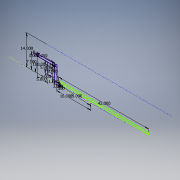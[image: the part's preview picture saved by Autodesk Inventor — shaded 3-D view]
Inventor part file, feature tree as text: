
AUTODESK INVENTOR PART (.ipt)
format: ipt  version: 2017 SP1 (Build 210196100, 196)  size: 114,688 bytes
history: native  units: in
note: dims shown in document units (in); Inventor stores cm internally (conversion verified against a paired STEP export)
features: sketch x1
ambient origin geometry x8: Origin, YZ Plane, XZ Plane, XY Plane, X Axis, Y Axis, Z Axis, Center Point
feature tree (1):
  sketch  "Sketch1"  dims[d0=5.0in d1=2.0in d3=1.0in d4=5.0in d5=7.5in d7=8.25in d10=1.25in d11=3.25in d13=42.0in d16=14.0in d19=3.0in d21=8.0in d22=0.0in d26=0.5in d27=0.5in d28=1.0in d29=15.0in d30=16.0in]
